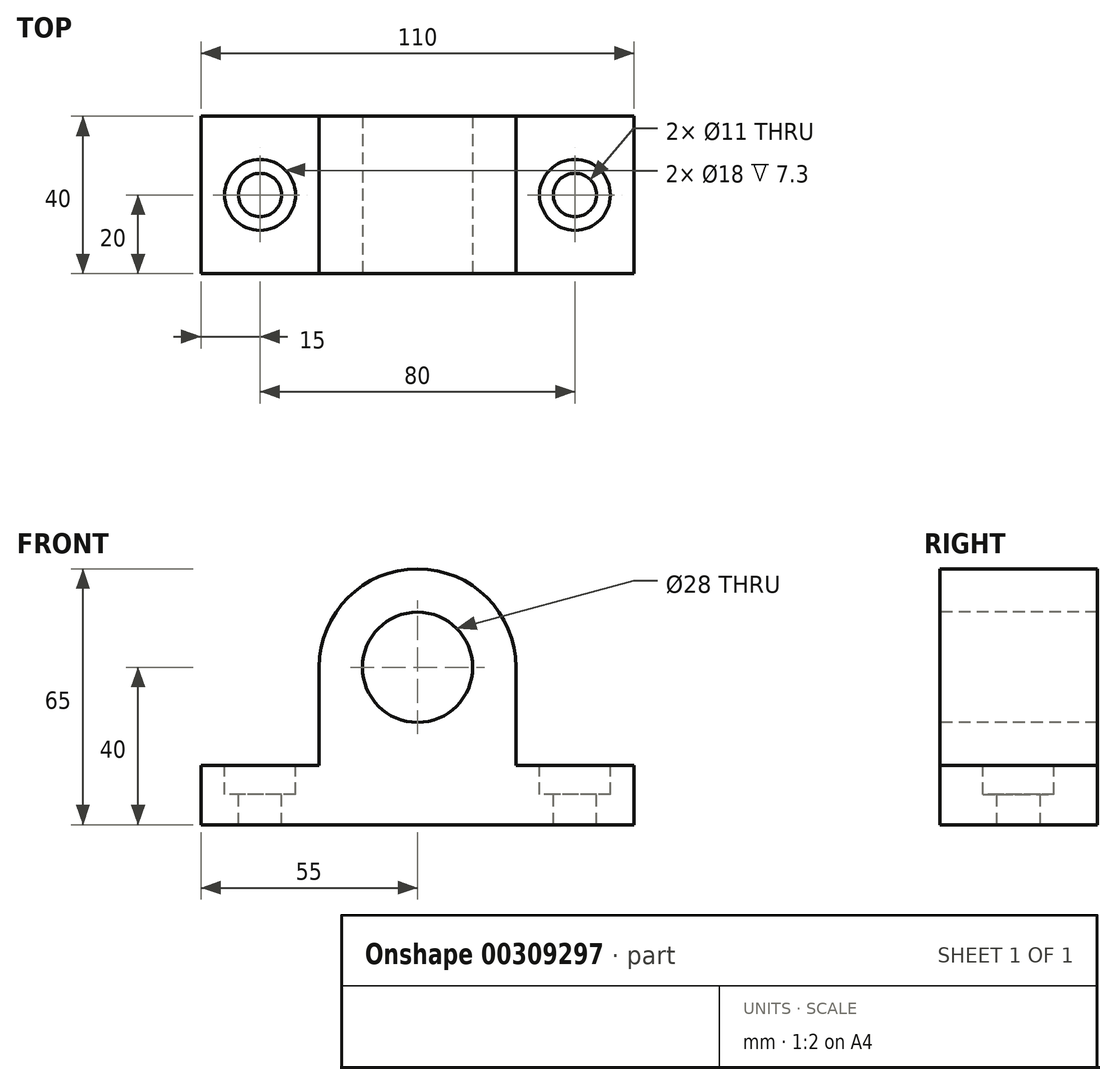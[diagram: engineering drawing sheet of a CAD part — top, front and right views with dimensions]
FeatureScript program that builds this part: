
annotation { "Feature Type Name" : "Feature", "Feature Type Description" : "" }
export const myFeature = defineFeature(function(context is Context, id is Id, definition is map)
    precondition{}
    {
        {
            var Q0;
            Q0=qCreatedBy(makeId("Top.planeOp"),FACE);
            var sketch = newSketch(context, id + "F0", { "sketchPlane" : qUnion([Q0])});
            skLineSegment(sketch, "E0.bottom", {"start": v(-55, -20) * mm, "end": v(55, -20) * mm});
            skLineSegment(sketch, "E0.top", {"start": v(-55, 20) * mm, "end": v(55, 20) * mm});
            skLineSegment(sketch, "E0.left", {"start": v(-55, -20) * mm, "end": v(-55, 20) * mm});
            skLineSegment(sketch, "E0.right", {"start": v(55, -20) * mm, "end": v(55, 20) * mm});
            skPoint(sketch, "E0.middle", {"position": v(0, 0) * mm});
            skSolve(sketch);
        }
        {
            var Q0;
            Q0=makeQuery(id+"F0.imprint","IMPRINT",FACE,{"disambiguationData":[TD([[makeQuery(id+"F0.imprint","IMPRINT",EDGE,{"derivedFrom":sQuery(id+"F0.wireOp",EDGE,"E0.bottom")}),1.0]])]});
            extrude(context, id + "F1", {"entities" : qUnion([Q0]), "depth" : 65 * mm});
        }
        {
            var Q0;
            Q0=makeQuery(id+"F1.opExtrude","CAP_FACE",FACE,{"disambiguationData":[OSD([sQuery(id+"F0.wireOp",EDGE,"E0.bottom"),sQuery(id+"F0.wireOp",EDGE,"E0.top"),sQuery(id+"F0.wireOp",EDGE,"E0.left"),sQuery(id+"F0.wireOp",EDGE,"E0.right")])],"isStart":false});
            var sketch = newSketch(context, id + "F2", { "sketchPlane" : qUnion([Q0])});
            skCircle(sketch, "E1", {"center": v(-40, 0) * mm, "radius": 5.5 * mm});
            skPoint(sketch, "E1.centerSnap0", {"position": v(-55, 0) * mm});
            skCircle(sketch, "E2", {"center": v(40, 0) * mm, "radius": 5.5 * mm});
            skCircle(sketch, "E3", {"center": v(-40, 0) * mm, "radius": 9 * mm});
            skCircle(sketch, "E4", {"center": v(40, 0) * mm, "radius": 9 * mm});
            skSolve(sketch);
        }
        {
            var Q0;
            Q0=makeQuery(id+"F2.imprint","IMPRINT",FACE,{"disambiguationData":[TD([[makeQuery(id+"F2.imprint","IMPRINT",EDGE,{"derivedFrom":sQuery(id+"F2.wireOp",EDGE,"E1")}),1.0]])]});
            var Q1;
            Q1=makeQuery(id+"F2.imprint","IMPRINT",FACE,{"disambiguationData":[TD([[makeQuery(id+"F2.imprint","IMPRINT",EDGE,{"derivedFrom":sQuery(id+"F2.wireOp",EDGE,"E2")}),1.0]])]});
            extrude(context, id + "F3", {"entities" : qUnion([Q0, Q1]), "operationType" : NewBodyOperationType.REMOVE, "oppositeDirection" : true, "depth" : 80 * mm});
        }
        {
            var Q0;
            Q0 = qSketchRegion(id + "F2", true);
            extrude(context, id + "F4", {"entities" : qUnion([Q0]), "operationType" : NewBodyOperationType.REMOVE, "oppositeDirection" : true, "depth" : 57.3 * mm});
        }
        {
            var Q0;
            Q0=makeQuery(id+"F1.opExtrude","SWEPT_FACE",FACE,{"disambiguationData":[OSD([sQuery(id+"F0.wireOp",EDGE,"E0.bottom")])]});
            var sketch = newSketch(context, id + "F5", { "sketchPlane" : qUnion([Q0])});
            skLineSegment(sketch, "E5", {"start": v(-55, 15) * mm, "end": v(-25, 15) * mm});
            skLineSegment(sketch, "E6", {"start": v(-25, 15) * mm, "end": v(-25, 44.02) * mm});
            skLineSegment(sketch, "E7", {"start": v(25, 44.02) * mm, "end": v(25, 15) * mm});
            skLineSegment(sketch, "E8", {"start": v(25, 15) * mm, "end": v(55, 15) * mm});
            skCircle(sketch, "E9", {"center": v(0, 40) * mm, "radius": 25 * mm});
            skCircle(sketch, "E10", {"center": v(0, 40) * mm, "radius": 14 * mm});
            skSolve(sketch);
        }
        {
            var Q0;
            Q0=makeQuery(id+"F5.imprint","IMPRINT",FACE,{"disambiguationData":[TD([[makeQuery(id+"F5.imprint","IMPRINT",EDGE,{"derivedFrom":sQuery(id+"F5.wireOp",EDGE,"E10")}),1.0]])]});
            var Q1;
            {var subQ1=sQuery(id+"F5.wireOp",EDGE,"E5");Q1=makeQuery(id+"F5.imprint","IMPRINT",FACE,{"disambiguationData":[TD([[makeQuery(id+"F5.imprint","IMPRINT",EDGE,{"derivedFrom":subQ1}),1.0]])]});}
            var Q2;
            {var subQ6=sQuery(id+"F5.wireOp",EDGE,"E8");Q2=makeQuery(id+"F5.imprint","IMPRINT",FACE,{"disambiguationData":[TD([[makeQuery(id+"F5.imprint","IMPRINT",EDGE,{"derivedFrom":subQ6}),1.0]])]});}
            extrude(context, id + "F6", {"entities" : qUnion([Q0, Q1, Q2]), "operationType" : NewBodyOperationType.REMOVE, "oppositeDirection" : true, "depth" : 80 * mm});
        }
    });
